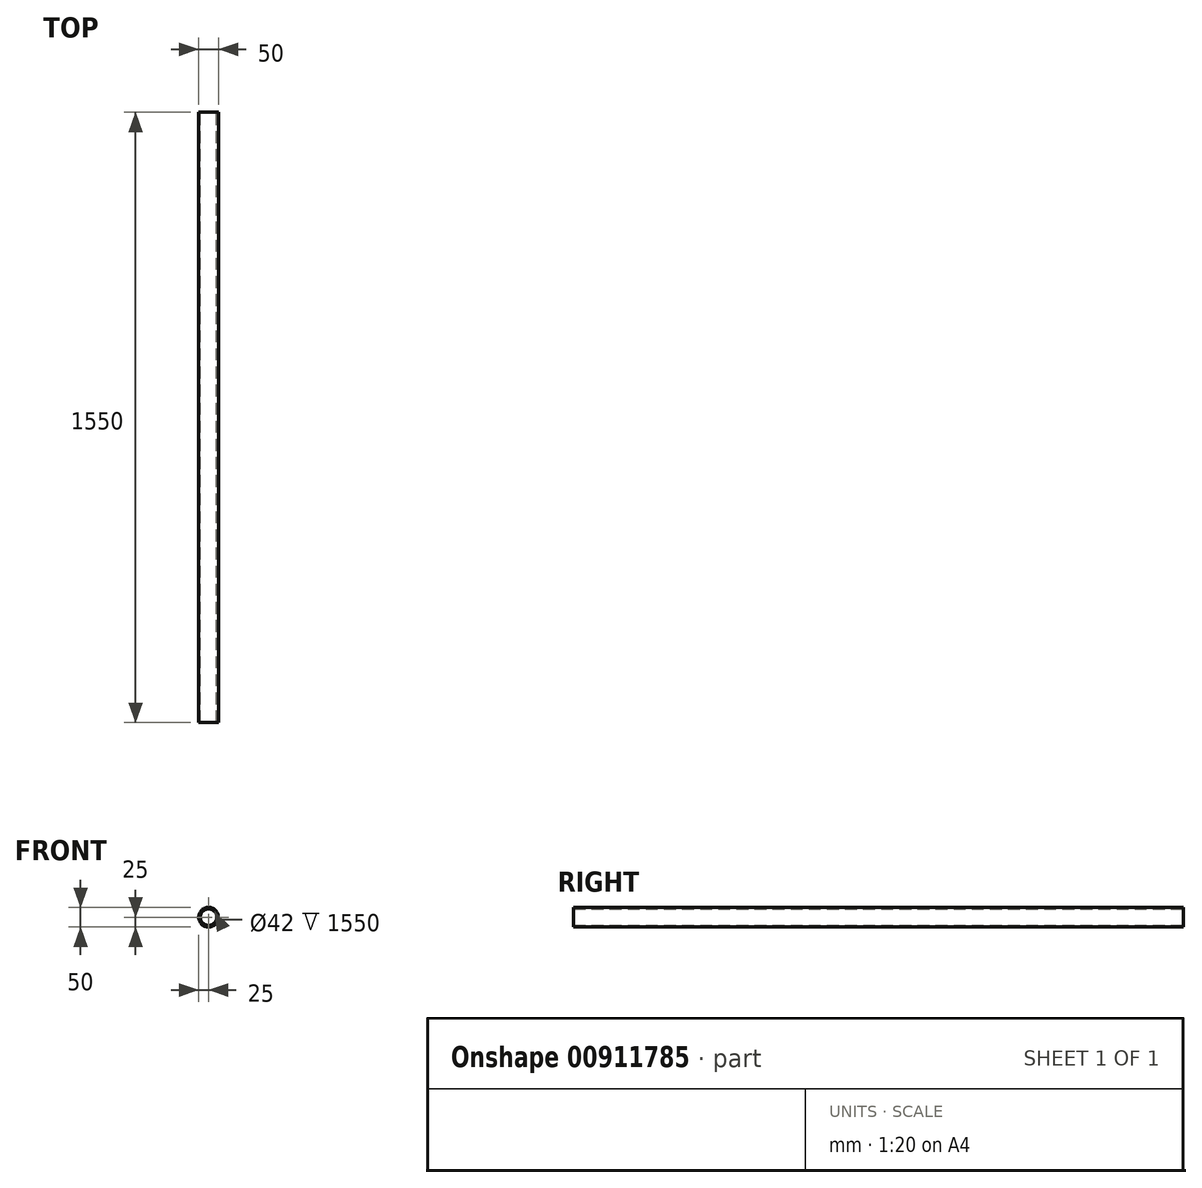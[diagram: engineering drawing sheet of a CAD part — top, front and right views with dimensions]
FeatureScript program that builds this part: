
annotation { "Feature Type Name" : "Feature", "Feature Type Description" : "" }
export const myFeature = defineFeature(function(context is Context, id is Id, definition is map)
    precondition{}
    {
        {
            var Q0;
            Q0=qCreatedBy(makeId("Front.planeOp"),FACE);
            var sketch = newSketch(context, id + "F0", { "sketchPlane" : qUnion([Q0])});
            skCircle(sketch, "E0", {"center": v(0, 0) * mm, "radius": 25 * mm});
            skCircle(sketch, "E1", {"center": v(0, 0) * mm, "radius": 21 * mm});
            skSolve(sketch);
        }
        {
            var Q0;
            Q0=makeQuery(id+"F0.imprint","IMPRINT",FACE,{"disambiguationData":[TD([[makeQuery(id+"F0.imprint","IMPRINT",EDGE,{"derivedFrom":sQuery(id+"F0.wireOp",EDGE,"E0")}),1.0]])]});
            extrude(context, id + "F1", {"entities" : qUnion([Q0]), "depth" : 1500 * mm, "offsetDistance" : 25 * mm, "hasSecondDirection" : true, "secondDirectionOppositeDirection" : true, "secondDirectionDepth" : 50 * mm});
        }
    });
